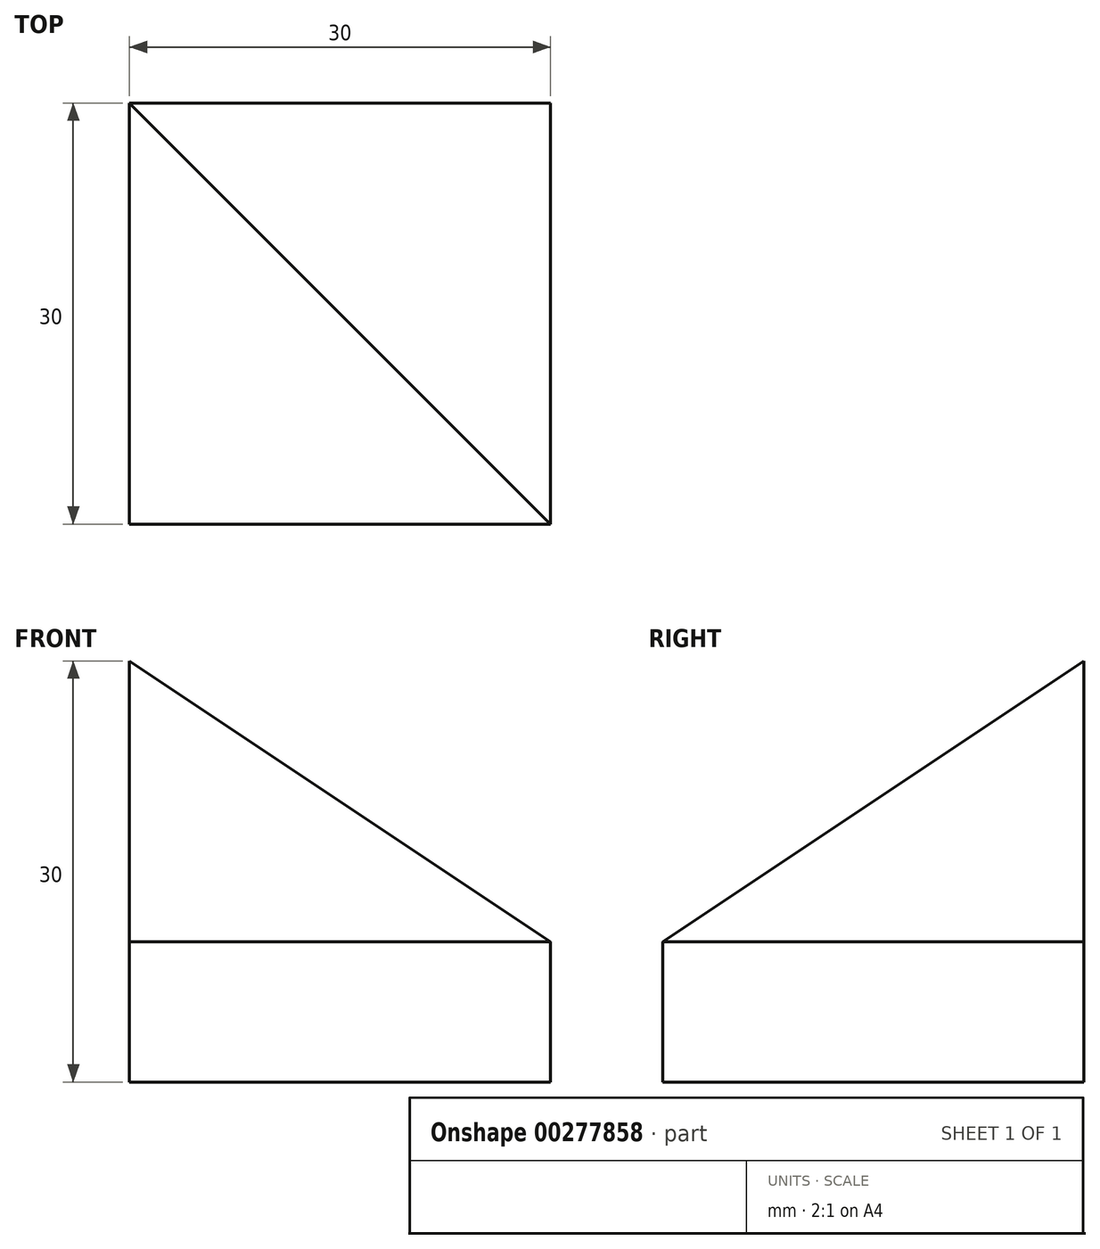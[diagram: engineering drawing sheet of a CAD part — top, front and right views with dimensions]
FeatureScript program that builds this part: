
annotation { "Feature Type Name" : "Feature", "Feature Type Description" : "" }
export const myFeature = defineFeature(function(context is Context, id is Id, definition is map)
    precondition{}
    {
        {
            var Q0;
            Q0=qCreatedBy(makeId("Front.planeOp"),FACE);
            var sketch = newSketch(context, id + "F0", { "sketchPlane" : qUnion([Q0])});
            skLineSegment(sketch, "E0.bottom", {"start": v(0, 0) * mm, "end": v(30, 0) * mm});
            skLineSegment(sketch, "E0.left", {"start": v(0, 0) * mm, "end": v(0, 30) * mm});
            skLineSegment(sketch, "E0.right", {"start": v(30, 0) * mm, "end": v(30, 10) * mm});
            skLineSegment(sketch, "E1", {"start": v(0, 30) * mm, "end": v(30, 10) * mm});
            skSolve(sketch);
        }
        {
            var Q0;
            Q0 = qSketchRegion(id + "F0", true);
            extrude(context, id + "F1", {"entities" : qUnion([Q0]), "depth" : 30 * mm});
        }
        {
            var Q0;
            Q0=makeQuery(id+"F1.opExtrude","SWEPT_FACE",FACE,{"disambiguationData":[OSD([sQuery(id+"F0.wireOp",EDGE,"E0.left")])]});
            var sketch = newSketch(context, id + "F2", { "sketchPlane" : qUnion([Q0])});
            skLineSegment(sketch, "E2.0", {"start": v(30, 30) * mm, "end": v(0, 30) * mm});
            skLineSegment(sketch, "E3.0", {"start": v(30, 0) * mm, "end": v(30, 30) * mm});
            skLineSegment(sketch, "E4.0", {"start": v(30, 10) * mm, "end": v(0, 10) * mm});
            skLineSegment(sketch, "E5", {"start": v(0, 30) * mm, "end": v(30, 10) * mm});
            skSolve(sketch);
        }
        {
            var Q0;
            Q0 = qSketchRegion(id + "F2", true);
            extrude(context, id + "F3", {"entities" : qUnion([Q0]), "operationType" : NewBodyOperationType.REMOVE, "endBound" : BoundingType.THROUGH_ALL, "oppositeDirection" : true, "depth" : 30 * mm});
        }
    });
